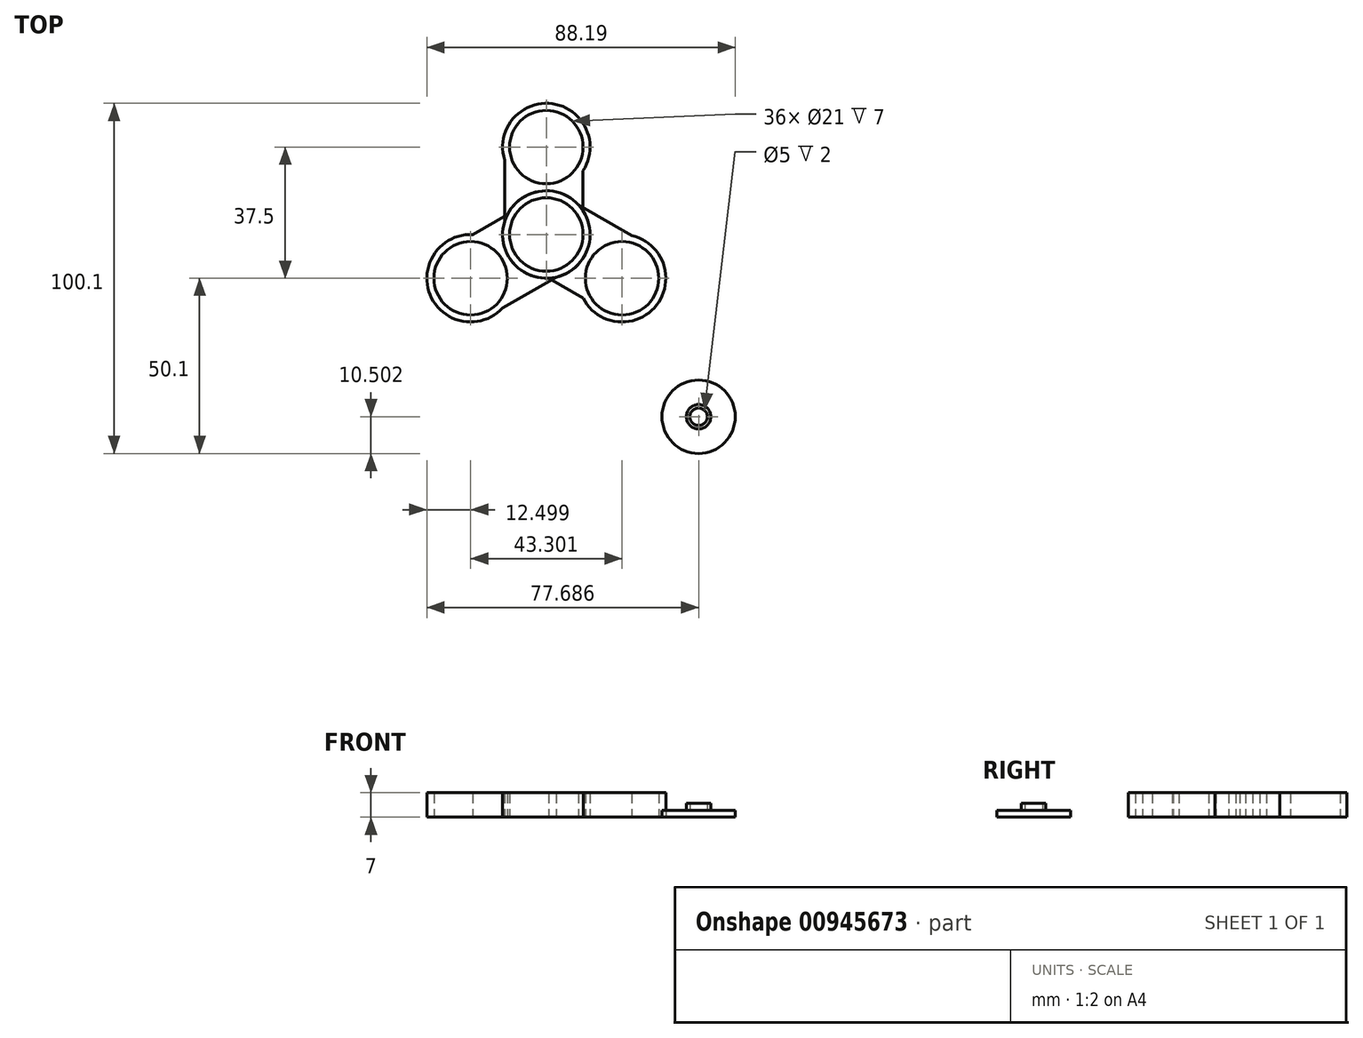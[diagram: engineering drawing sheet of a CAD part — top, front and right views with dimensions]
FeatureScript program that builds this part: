
annotation { "Feature Type Name" : "Feature", "Feature Type Description" : "" }
export const myFeature = defineFeature(function(context is Context, id is Id, definition is map)
    precondition{}
    {
        {
            var Q0;
            Q0=qCreatedBy(makeId("Top.planeOp"),FACE);
            var sketch = newSketch(context, id + "F0", { "sketchPlane" : qUnion([Q0])});
            skCircle(sketch, "E0", {"center": v(0, 0) * mm, "radius": 10.5 * mm});
            skPoint(sketch, "E1.center.orphan", {"position": v(0, 21) * mm});
            skCircle(sketch, "E2.0", {"center": v(0, 0) * mm, "radius": 12.5 * mm});
            skCircle(sketch, "E3", {"center": v(0, 25) * mm, "radius": 10.5 * mm});
            skCircle(sketch, "E4.0", {"center": v(0, 25) * mm, "radius": 12.5 * mm});
            skLineSegment(sketch, "E5", {"start": v(-11.94, 21.3) * mm, "end": v(-11.94, 3.7) * mm});
            skLineSegment(sketch, "E6", {"start": v(10.5, 18.22) * mm, "end": v(10.5, 6.78) * mm});
            skCircle(sketch, "E7", {"center": v(43.54, -52.1) * mm, "radius": 10.5 * mm});
            skCircle(sketch, "E8", {"center": v(43.54, -52.1) * mm, "radius": 3.5 * mm});
            skCircle(sketch, "E9", {"center": v(43.54, -52.1) * mm, "radius": 2.5 * mm});
            skSolve(sketch);
        }
        {
            var Q0;
            {var subQ0=sQuery(id+"F0.wireOp",EDGE,"E5");Q0=makeQuery(id+"F0.imprint","IMPRINT",FACE,{"disambiguationData":[TD([[makeQuery(id+"F0.imprint","IMPRINT",EDGE,{"derivedFrom":subQ0}),1.0]])]});}
            var Q1;
            {var subQ0=sQuery(id+"F0.wireOp",EDGE,"E6");Q1=makeQuery(id+"F0.imprint","IMPRINT",FACE,{"disambiguationData":[TD([[makeQuery(id+"F0.imprint","IMPRINT",EDGE,{"derivedFrom":subQ0}),-1.0]])]});}
            var Q2;
            Q2=makeQuery(id+"F0.imprint","IMPRINT",FACE,{"disambiguationData":[TD([[makeQuery(id+"F0.imprint","IMPRINT",EDGE,{"derivedFrom":sQuery(id+"F0.wireOp",EDGE,"E3")}),-1.0]])]});
            var Q3;
            Q3=makeQuery(id+"F0.imprint","IMPRINT",FACE,{"disambiguationData":[TD([[makeQuery(id+"F0.imprint","IMPRINT",EDGE,{"derivedFrom":sQuery(id+"F0.wireOp",EDGE,"E0")}),-1.0]])]});
            extrude(context, id + "F1", {"entities" : qUnion([Q0, Q1, Q2, Q3]), "depth" : 7 * mm, "offsetDistance" : 25 * mm});
        }
        {
            var Q0;
            Q0=makeQuery(id+"F1.opExtrude","SWEPT_BODY",BODY,{"disambiguationData":[OSD([sQuery(id+"F0.wireOp",EDGE,"E0"),sQuery(id+"F0.wireOp",EDGE,"E2.0"),sQuery(id+"F0.wireOp",EDGE,"E3"),sQuery(id+"F0.wireOp",EDGE,"E4.0"),sQuery(id+"F0.wireOp",EDGE,"E5"),sQuery(id+"F0.wireOp",EDGE,"E6")])]});
            var Q1;
            Q1=makeQuery(id+"F1.opExtrude","CAP_EDGE",EDGE,{"disambiguationData":[OSD([sQuery(id+"F0.wireOp",EDGE,"E0")])],"isStart":false});
            circularPattern(context, id + "F2", {"entities" : qUnion([Q0]), "axis" : qUnion([Q1]), "angle" : 360 * degree, "instanceCount" : 3, "equalSpace" : true});
        }
        {
            var Q0;
            Q0=makeQuery(id+"F0.imprint","IMPRINT",FACE,{"disambiguationData":[TD([[makeQuery(id+"F0.imprint","IMPRINT",EDGE,{"derivedFrom":sQuery(id+"F0.wireOp",EDGE,"E7")}),1.0]])]});
            extrude(context, id + "F3", {"entities" : qUnion([Q0]), "depth" : 2 * mm, "offsetDistance" : 25 * mm});
        }
        {
            var Q0;
            Q0=makeQuery(id+"F0.imprint","IMPRINT",FACE,{"disambiguationData":[TD([[makeQuery(id+"F0.imprint","IMPRINT",EDGE,{"derivedFrom":sQuery(id+"F0.wireOp",EDGE,"E8")}),1.0]])]});
            extrude(context, id + "F4", {"entities" : qUnion([Q0]), "operationType" : NewBodyOperationType.ADD, "depth" : 4 * mm, "offsetDistance" : 25 * mm});
        }
        {
            var Q0;
            Q0=makeQuery(id+"F0.imprint","IMPRINT",FACE,{"disambiguationData":[TD([[makeQuery(id+"F0.imprint","IMPRINT",EDGE,{"derivedFrom":sQuery(id+"F0.wireOp",EDGE,"E9")}),1.0]])]});
            extrude(context, id + "F5", {"entities" : qUnion([Q0]), "operationType" : NewBodyOperationType.ADD, "depth" : 2 * mm, "offsetDistance" : 25 * mm});
        }
    });
